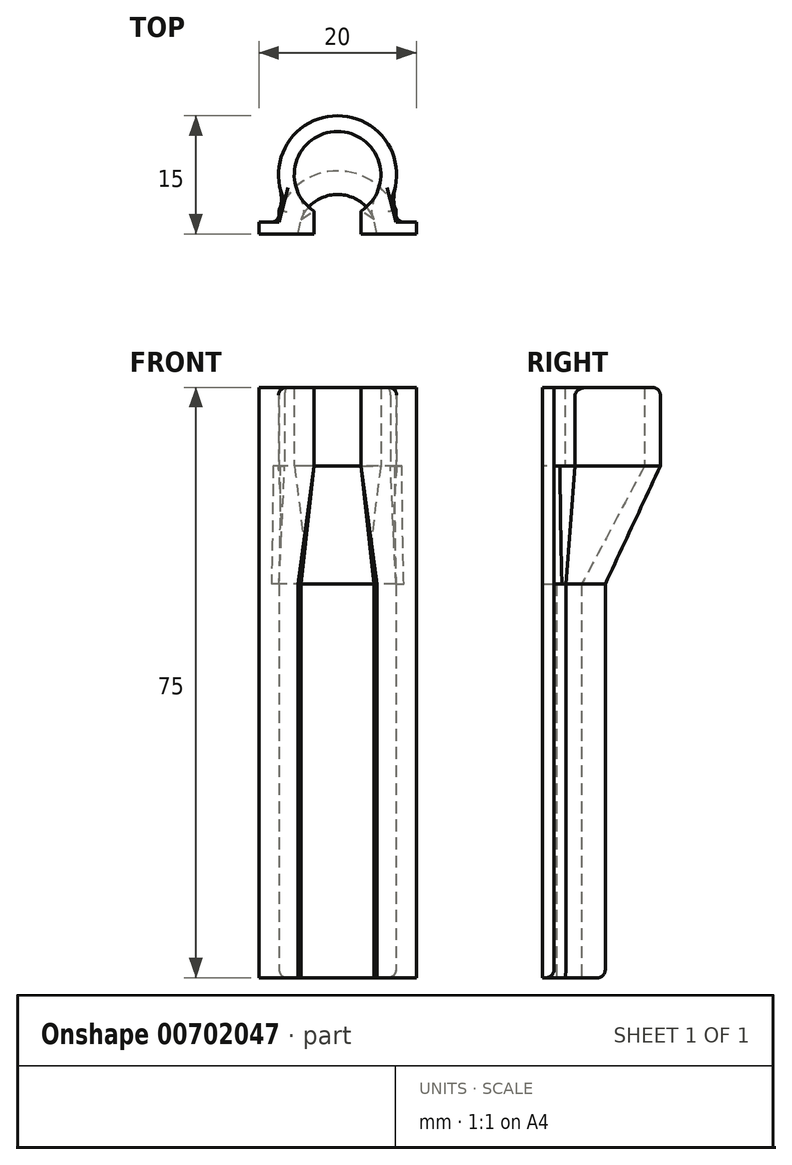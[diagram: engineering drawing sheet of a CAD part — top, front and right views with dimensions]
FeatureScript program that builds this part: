
annotation { "Feature Type Name" : "Feature", "Feature Type Description" : "" }
export const myFeature = defineFeature(function(context is Context, id is Id, definition is map)
    precondition{}
    {
        {
            var Q0;
            Q0=qCreatedBy(makeId("Top.planeOp"),FACE);
            var sketch = newSketch(context, id + "F0", { "sketchPlane" : qUnion([Q0])});
            skArc(sketch, "E0", {"start": v(14.66, 1.82) * mm, "mid": v(10, 5) * mm, "end": v(5.34, 1.82) * mm});
            skLineSegment(sketch, "E1", {"start": v(0, 0) * mm, "end": v(5, 0) * mm});
            skLineSegment(sketch, "E2.trimOffspring", {"start": v(15, 0) * mm, "end": v(20, 0) * mm});
            skArc(sketch, "E3.1", {"start": v(17.42, 3) * mm, "mid": v(10, 8) * mm, "end": v(2.58, 3) * mm});
            skLineSegment(sketch, "E4", {"start": v(20, 0) * mm, "end": v(20, 1.5) * mm});
            skLineSegment(sketch, "E5", {"start": v(0, 0) * mm, "end": v(0, 1.5) * mm});
            skLineSegment(sketch, "E6", {"start": v(0, 1.5) * mm, "end": v(2.58, 1.5) * mm});
            skLineSegment(sketch, "E7", {"start": v(2.58, 1.5) * mm, "end": v(2.58, 3) * mm});
            skLineSegment(sketch, "E8", {"start": v(10, 0) * mm, "end": v(10, 12.25) * mm, "construction": true});
            skLineSegment(sketch, "E9.MirrorCS", {"start": v(17.42, 1.5) * mm, "end": v(17.42, 3) * mm});
            skLineSegment(sketch, "E10.MirrorCS", {"start": v(20, 1.5) * mm, "end": v(17.42, 1.5) * mm});
            skPoint(sketch, "E3.2.start.orphan", {"position": v(0, 3) * mm});
            skLineSegment(sketch, "E11", {"start": v(5, 0) * mm, "end": v(5.34, 1.82) * mm});
            skLineSegment(sketch, "E12.MirrorCS", {"start": v(15, 0) * mm, "end": v(14.66, 1.82) * mm});
            skSolve(sketch);
        }
        {
            var Q0;
            Q0 = qSketchRegion(id + "F0", true);
            extrude(context, id + "F1", {"entities" : qUnion([Q0]), "depth" : 50 * mm, "offsetDistance" : 25 * mm});
        }
        {
            var Q0;
            Q0=makeQuery(id+"F1.opExtrude","CAP_FACE",FACE,{"disambiguationData":[OSD([sQuery(id+"F0.wireOp",EDGE,"E0"),sQuery(id+"F0.wireOp",EDGE,"E1"),sQuery(id+"F0.wireOp",EDGE,"E2.trimOffspring"),sQuery(id+"F0.wireOp",EDGE,"E3.0"),sQuery(id+"F0.wireOp",EDGE,"E3.1"),sQuery(id+"F0.wireOp",EDGE,"E3.2"),sQuery(id+"F0.wireOp",EDGE,"E4"),sQuery(id+"F0.wireOp",EDGE,"E5")])],"isStart":false});
            cPlane(context, id + "F2", {"entities" : qUnion([Q0]), "cplaneType" : CPlaneType.OFFSET, "offset" : 15 * mm, "width" : 150 * mm, "height" : 150 * mm});
        }
        {
            var Q0;
            Q0=qCreatedBy(id+"F2.planeOp",FACE);
            var sketch = newSketch(context, id + "F3", { "sketchPlane" : qUnion([Q0])});
            skArc(sketch, "E13", {"start": v(16.72, 4.17) * mm, "mid": v(10, 15) * mm, "end": v(3.28, 4.17) * mm});
            skArc(sketch, "E14", {"start": v(13, 2.9) * mm, "mid": v(10, 13) * mm, "end": v(7, 2.9) * mm});
            skLineSegment(sketch, "E15", {"start": v(4.5, 0) * mm, "end": v(4.5, 0) * mm});
            skPoint(sketch, "E16.orphan", {"position": v(7, 0) * mm});
            skLineSegment(sketch, "E17.top", {"start": v(2.58, 1.5) * mm, "end": v(0, 1.5) * mm});
            skLineSegment(sketch, "E17.right", {"start": v(0, 0) * mm, "end": v(0, 1.5) * mm});
            skLineSegment(sketch, "E18.MirrorCS", {"start": v(20, 0) * mm, "end": v(20, 1.5) * mm});
            skLineSegment(sketch, "E19.MirrorCS", {"start": v(17.42, 1.5) * mm, "end": v(20, 1.5) * mm});
            skPoint(sketch, "E20.start.orphan", {"position": v(2.58, 2.9) * mm});
            skLineSegment(sketch, "E21", {"start": v(3.28, 4.17) * mm, "end": v(2.58, 1.5) * mm});
            skPoint(sketch, "E22.MirrorCS.start.orphan", {"position": v(17.42, 2.9) * mm});
            skPoint(sketch, "E23.MirrorCS.end.orphan", {"position": v(17.42, 1.5) * mm});
            skLineSegment(sketch, "E24", {"start": v(17.42, 1.5) * mm, "end": v(16.72, 4.17) * mm});
            skPoint(sketch, "E25.orphan", {"position": v(7, 0.63) * mm});
            skPoint(sketch, "E17.bottom.start.orphan", {"position": v(2.58, 0) * mm});
            skPoint(sketch, "E26.MirrorCS.end.orphan", {"position": v(13, 2.9) * mm});
            skPoint(sketch, "E27.right.end.orphan", {"position": v(13, 0.63) * mm});
            skPoint(sketch, "E28.MirrorCS.end.orphan", {"position": v(17.42, 0) * mm});
            skPoint(sketch, "E28.MirrorCS.start.orphan", {"position": v(13, 0) * mm});
            skPoint(sketch, "E29.MirrorCS.end.orphan", {"position": v(20, 0) * mm});
            skLineSegment(sketch, "E30", {"start": v(0, 0) * mm, "end": v(7, 0) * mm});
            skLineSegment(sketch, "E31", {"start": v(7, 2.9) * mm, "end": v(7, 0) * mm});
            skLineSegment(sketch, "E32", {"start": v(13, 2.9) * mm, "end": v(13, 0) * mm});
            skLineSegment(sketch, "E33", {"start": v(13, 0) * mm, "end": v(20, 0) * mm});
            skSolve(sketch);
        }
        {
            var Q0;
            Q0=makeQuery(id+"F1.opExtrude","CAP_FACE",FACE,{"disambiguationData":[OSD([sQuery(id+"F0.wireOp",EDGE,"E0"),sQuery(id+"F0.wireOp",EDGE,"E1"),sQuery(id+"F0.wireOp",EDGE,"E2.trimOffspring"),sQuery(id+"F0.wireOp",EDGE,"E3.1"),sQuery(id+"F0.wireOp",EDGE,"E4"),sQuery(id+"F0.wireOp",EDGE,"E5"),sQuery(id+"F0.wireOp",EDGE,"E6"),sQuery(id+"F0.wireOp",EDGE,"E7"),sQuery(id+"F0.wireOp",EDGE,"E9.MirrorCS"),sQuery(id+"F0.wireOp",EDGE,"E10.MirrorCS")])],"isStart":false});
            var Q1;
            Q1=makeQuery(id+"F3.imprint","IMPRINT",FACE,{"disambiguationData":[TD([[makeQuery(id+"F3.imprint","IMPRINT",EDGE,{"derivedFrom":sQuery(id+"F3.wireOp",EDGE,"E13")}),1.0]])]});
            var Q2;
            Q2=sQuery(id+"F3.wireOp",EDGE,"bKBu1X0q-kmc7-OAZN-VyrF-IS3qqaHm8IaW");
            var Q3;
            Q3=makeQuery(id+"F1.opExtrude","CAP_EDGE",EDGE,{"disambiguationData":[OSD([sQuery(id+"F0.wireOp",EDGE,"E9.MirrorCS")])],"isStart":false});
            loft(context, id + "F4", {"operationType" : NewBodyOperationType.ADD, "sheetProfilesArray" : [{ "sheetProfileEntities" : qUnion([Q0]) }, { "sheetProfileEntities" : qUnion([Q1]) }], "wireProfilesArray" : [{ "wireProfileEntities" : qUnion([Q2]) }, { "wireProfileEntities" : qUnion([Q3]) }]});
        }
        {
            var Q0;
            Q0=qCreatedBy(makeId("Right.planeOp"),FACE);
            cPlane(context, id + "F5", {"entities" : qUnion([Q0]), "cplaneType" : CPlaneType.OFFSET, "offset" : 25 * mm, "width" : 150 * mm, "height" : 150 * mm});
        }
        {
            var Q0;
            Q0=makeQuery(id+"F1.opExtrude","CAP_EDGE",EDGE,{"disambiguationData":[OSD([sQuery(id+"F0.wireOp",EDGE,"E3.1")])],"isStart":true});
            var Q1;
            Q1=makeQuery(id+"F1.opExtrude","CAP_EDGE",EDGE,{"disambiguationData":[OSD([sQuery(id+"F0.wireOp",EDGE,"E9.MirrorCS")])],"isStart":true});
            var Q2;
            Q2=makeQuery(id+"F1.opExtrude","CAP_EDGE",EDGE,{"disambiguationData":[OSD([sQuery(id+"F0.wireOp",EDGE,"E7")])],"isStart":true});
            fillet(context, id + "F6", {"entities" : qUnion([Q0, Q1, Q2]), "radius" : 1 * mm, "tangentPropagation" : true, "allowEdgeOverflow" : false});
        }
        {
            var Q0;
            Q0=makeQuery(id+"F1.opExtrude","CAP_EDGE",EDGE,{"disambiguationData":[OSD([sQuery(id+"F0.wireOp",EDGE,"E6")])],"isStart":true});
            var Q1;
            Q1=makeQuery(id+"F1.opExtrude","CAP_EDGE",EDGE,{"disambiguationData":[OSD([sQuery(id+"F0.wireOp",EDGE,"E10.MirrorCS")])],"isStart":true});
            var Q2;
            Q2=makeQuery(id+"F1.opExtrude","SWEPT_EDGE",EDGE,{"disambiguationData":[OSD([sQuery(id+"F0.wireOp",EDGE,"E6"),sQuery(id+"F0.wireOp",EDGE,"E7")])]});
            var Q3;
            Q3=makeQuery(id+"F1.opExtrude","SWEPT_EDGE",EDGE,{"disambiguationData":[OSD([sQuery(id+"F0.wireOp",EDGE,"E9.MirrorCS"),sQuery(id+"F0.wireOp",EDGE,"E10.MirrorCS")])]});
            fillet(context, id + "F7", {"entities" : qUnion([Q0, Q1, Q2, Q3]), "radius" : 1 * mm, "tangentPropagation" : true, "defaultsChanged" : false, "vertexSettings" : [], "allowEdgeOverflow" : false});
        }
        {
            var Q0;
            Q0=makeQuery(id+"F3.imprint","IMPRINT",FACE,{"disambiguationData":[TD([[makeQuery(id+"F3.imprint","IMPRINT",EDGE,{"derivedFrom":sQuery(id+"F3.wireOp",EDGE,"E13")}),1.0]])]});
            var Q1;
            Q1 = qSketchRegion(id + "F3", true);
            extrude(context, id + "F8", {"entities" : qUnion([Q0, Q1]), "operationType" : NewBodyOperationType.ADD, "depth" : 10 * mm, "offsetDistance" : 25 * mm});
        }
        {
            var Q0;
            Q0=makeQuery(id+"F8.opExtrude","CAP_EDGE",EDGE,{"disambiguationData":[OSD([sQuery(id+"F3.wireOp",EDGE,"E13")])],"isStart":false});
            fillet(context, id + "F9", {"entities" : qUnion([Q0]), "tangentPropagation" : true, "radius" : 1 * mm, "defaultsChanged" : true, "vertexSettings" : [], "allowEdgeOverflow" : false});
        }
    });
